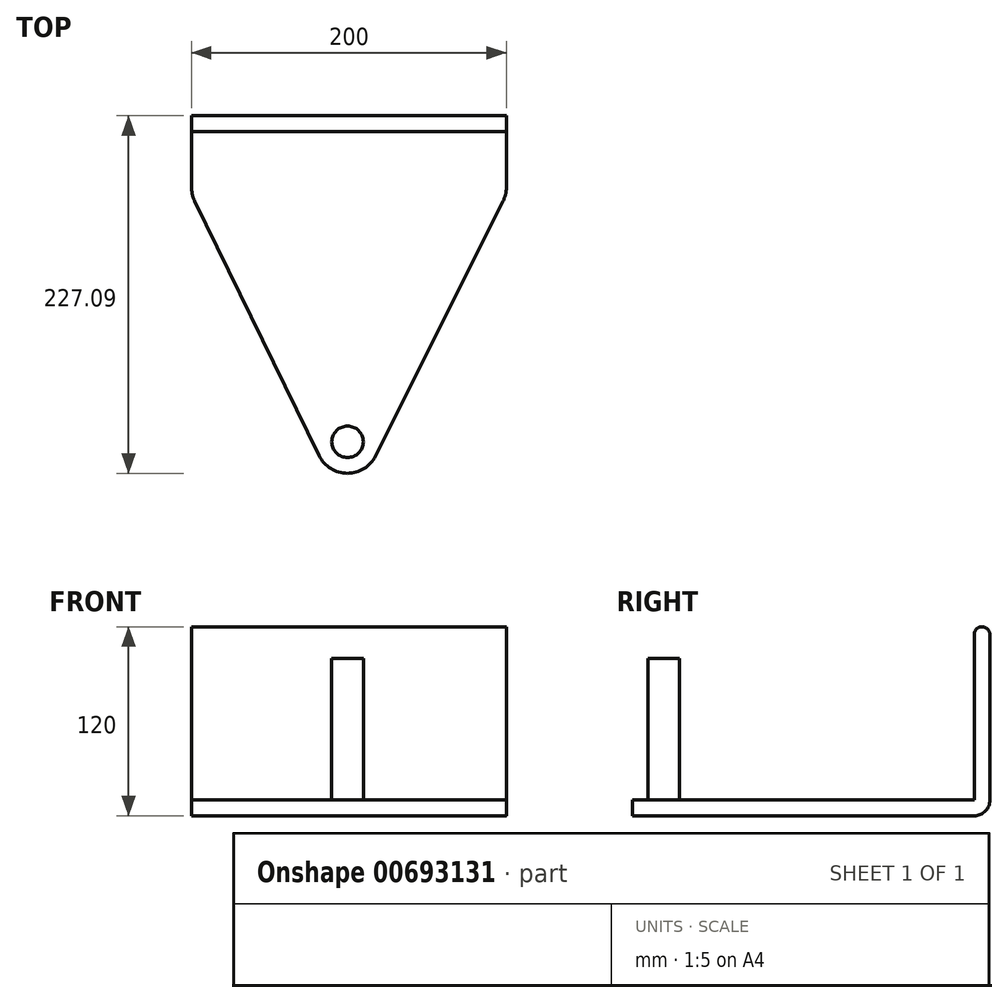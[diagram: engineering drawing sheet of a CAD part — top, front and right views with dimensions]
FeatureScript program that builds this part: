
annotation { "Feature Type Name" : "Feature", "Feature Type Description" : "" }
export const myFeature = defineFeature(function(context is Context, id is Id, definition is map)
    precondition{}
    {
        {
            var Q0;
            Q0=qCreatedBy(makeId("Top.planeOp"),FACE);
            var sketch = newSketch(context, id + "F0", { "sketchPlane" : qUnion([Q0])});
            skLineSegment(sketch, "E0", {"start": v(0, 0) * mm, "end": v(200, 0) * mm});
            skLineSegment(sketch, "E1", {"start": v(200, 0) * mm, "end": v(98.9, -202.2) * mm});
            skLineSegment(sketch, "E2", {"start": v(98.9, -202.2) * mm, "end": v(0, 0) * mm});
            skLineSegment(sketch, "E3", {"start": v(100, -200) * mm, "end": v(100, 0) * mm, "construction": true});
            skPoint(sketch, "E3.endSnap0", {"position": v(100, 0) * mm});
            skLineSegment(sketch, "E4.top", {"start": v(0, 50) * mm, "end": v(200, 50) * mm});
            skLineSegment(sketch, "E4.left", {"start": v(0, 0) * mm, "end": v(0, 50) * mm});
            skLineSegment(sketch, "E4.right", {"start": v(200, 0) * mm, "end": v(200, 50) * mm});
            skSolve(sketch);
        }
        {
            var Q0;
            Q0=makeQuery(id+"F0.imprint","IMPRINT",FACE,{"disambiguationData":[TD([[makeQuery(id+"F0.imprint","IMPRINT",EDGE,{"derivedFrom":sQuery(id+"F0.wireOp",EDGE,"E1")}),-1.0]])]});
            var Q1;
            Q1=makeQuery(id+"F0.imprint","IMPRINT",FACE,{"disambiguationData":[TD([[makeQuery(id+"F0.imprint","IMPRINT",EDGE,{"derivedFrom":sQuery(id+"F0.wireOp",EDGE,"E0")}),1.0]])]});
            extrude(context, id + "F1", {"entities" : qUnion([Q0, Q1]), "depth" : 10 * mm, "offsetDistance" : 25 * mm});
        }
        {
            var Q0;
            Q0=makeQuery(id+"F1.opExtrude","SWEPT_EDGE",EDGE,{"disambiguationData":[OSD([sQuery(id+"F0.wireOp",EDGE,"E1"),sQuery(id+"F0.wireOp",EDGE,"E2")])]});
            var Q1;
            Q1=makeQuery(id+"F1.opExtrude","SWEPT_EDGE",EDGE,{"disambiguationData":[OSD([sQuery(id+"F0.wireOp",EDGE,"E1"),sQuery(id+"F0.wireOp",EDGE,"E0"),sQuery(id+"F0.wireOp",EDGE,"E4.right")])]});
            var Q2;
            Q2=makeQuery(id+"F1.opExtrude","SWEPT_EDGE",EDGE,{"disambiguationData":[OSD([sQuery(id+"F0.wireOp",EDGE,"E2"),sQuery(id+"F0.wireOp",EDGE,"E0"),sQuery(id+"F0.wireOp",EDGE,"E4.left")])]});
            fillet(context, id + "F2", {"entities" : qUnion([Q0, Q1, Q2]), "radius" : 20 * mm, "tangentPropagation" : true, "allowEdgeOverflow" : false});
        }
        {
            var Q0;
            Q0=makeQuery(id+"F1.opExtrude","CAP_FACE",FACE,{"disambiguationData":[OSD([sQuery(id+"F0.wireOp",EDGE,"E1"),sQuery(id+"F0.wireOp",EDGE,"E2"),sQuery(id+"F0.wireOp",EDGE,"E4.top"),sQuery(id+"F0.wireOp",EDGE,"E4.left"),sQuery(id+"F0.wireOp",EDGE,"E4.right")])],"isStart":false});
            var sketch = newSketch(context, id + "F3", { "sketchPlane" : qUnion([Q0])});
            skCircle(sketch, "E5", {"center": v(99.1, -157.09) * mm, "radius": 10 * mm});
            skSolve(sketch);
        }
        {
            var Q0;
            Q0=makeQuery(id+"F3.imprint","IMPRINT",FACE,{"disambiguationData":[TD([[makeQuery(id+"F3.imprint","IMPRINT",EDGE,{"derivedFrom":sQuery(id+"F3.wireOp",EDGE,"E5")}),1.0]])]});
            extrude(context, id + "F4", {"entities" : qUnion([Q0]), "operationType" : NewBodyOperationType.ADD, "depth" : 90 * mm, "offsetDistance" : 25 * mm});
        }
        {
            var Q0;
            Q0=makeQuery(id+"F1.opExtrude","CAP_FACE",FACE,{"disambiguationData":[OSD([sQuery(id+"F0.wireOp",EDGE,"E1"),sQuery(id+"F0.wireOp",EDGE,"E2"),sQuery(id+"F0.wireOp",EDGE,"E4.top"),sQuery(id+"F0.wireOp",EDGE,"E4.left"),sQuery(id+"F0.wireOp",EDGE,"E4.right")])],"isStart":false});
            var sketch = newSketch(context, id + "F5", { "sketchPlane" : qUnion([Q0])});
            skLineSegment(sketch, "E6.bottom", {"start": v(0, 50) * mm, "end": v(200, 50) * mm});
            skLineSegment(sketch, "E6.top", {"start": v(0, 40) * mm, "end": v(200, 40) * mm});
            skLineSegment(sketch, "E6.left", {"start": v(0, 50) * mm, "end": v(0, 40) * mm});
            skLineSegment(sketch, "E6.right", {"start": v(200, 50) * mm, "end": v(200, 40) * mm});
            skSolve(sketch);
        }
        {
            var Q0;
            Q0=makeQuery(id+"F5.imprint","IMPRINT",FACE,{"disambiguationData":[TD([[makeQuery(id+"F5.imprint","IMPRINT",EDGE,{"derivedFrom":sQuery(id+"F5.wireOp",EDGE,"E6.bottom")}),-1.0]])]});
            extrude(context, id + "F6", {"entities" : qUnion([Q0]), "operationType" : NewBodyOperationType.ADD, "depth" : 110 * mm, "offsetDistance" : 25 * mm});
        }
        {
            var Q0;
            Q0=makeQuery(id+"F6.opExtrude","CAP_EDGE",EDGE,{"disambiguationData":[OSD([sQuery(id+"F5.wireOp",EDGE,"E6.bottom")])],"isStart":false});
            var Q1;
            Q1=makeQuery(id+"F6.opExtrude","CAP_EDGE",EDGE,{"disambiguationData":[OSD([sQuery(id+"F5.wireOp",EDGE,"E6.top")])],"isStart":false});
            var Q2;
            Q2=makeQuery(id+"F6.opExtrude","CAP_EDGE",EDGE,{"disambiguationData":[OSD([sQuery(id+"F5.wireOp",EDGE,"E6.top")])],"isStart":true});
            fillet(context, id + "F7", {"entities" : qUnion([Q0, Q1, Q2]), "radius" : 5 * mm, "tangentPropagation" : true, "allowEdgeOverflow" : false});
        }
        {
            var Q0;
            Q0=makeQuery(id+"F1.opExtrude","CAP_EDGE",EDGE,{"disambiguationData":[OSD([sQuery(id+"F0.wireOp",EDGE,"E4.top")])],"isStart":true});
            fillet(context, id + "F8", {"entities" : qUnion([Q0]), "radius" : 10 * mm, "tangentPropagation" : true, "allowEdgeOverflow" : false});
        }
    });
